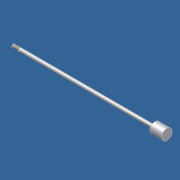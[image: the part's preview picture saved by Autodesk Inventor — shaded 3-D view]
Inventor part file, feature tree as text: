
AUTODESK INVENTOR PART (.ipt)
format: ipt  version: 2012 (Build 160160000, 160)  size: 124,928 bytes
history: native  units: in
note: dims shown in document units (in); Inventor stores cm internally (conversion verified against a paired STEP export)
features: other x84, revolve x3, sketch x3, thread x1
ambient origin geometry x8: Origin, YZ Plane, XZ Plane, XY Plane, X Axis, Y Axis, Z Axis, Center Point
bodies: Solid1 (feature_tree)
feature tree (91):
  revolve  "Revolution1"  Angle=360.0deg
  revolve  "Revolution2"  Angle=360.0deg
  thread  "Thread1"  [1 undecoded]
  revolve  "Revolution3"  [1 undecoded]
  other  "rod_cp_XY"
  other  "rod_cp_YZ"
  other  "rod_cp_ZX"
  other  "rod_cp_X"
  other  "rod_cp_Y"
  other  "rod_cp_Z"
  other  "rod_cp_Center"
  other  "to_rod_clevis_XY"
  other  "to_rod_clevis_YZ"
  other  "to_rod_clevis_ZX"
  other  "to_rod_clevis_X"
  other  "to_rod_clevis_Y"
  other  "to_rod_clevis_Z"
  other  "to_rod_clevis_Center"
  other  "rl2_XY"
  other  "rl2_YZ"
  other  "rl2_ZX"
  other  "rl2_X"
  other  "rl2_Y"
  other  "rl2_Z"
  other  "rl2_Center"
  other  "rl1_XY"
  other  "rl1_YZ"
  other  "rl1_ZX"
  other  "rl1_X"
  other  "rl1_Y"
  other  "rl1_Z"
  other  "rl1_Center"
  other  "thd1_XY"
  other  "thd1_YZ"
  other  "thd1_ZX"
  other  "thd1_X"
  other  "thd1_Y"
  other  "thd1_Z"
  other  "thd1_Center"
  other  "thd2_XY"
  other  "thd2_YZ"
  other  "thd2_ZX"
  other  "thd2_X"
  other  "thd2_Y"
  other  "thd2_Z"
  other  "thd2_Center"
  other  "dia1_XY"
  other  "dia1_YZ"
  other  "dia1_ZX"
  other  "dia1_X"
  other  "dia1_Y"
  other  "dia1_Z"
  other  "dia1_Center"
  other  "dia2_XY"
  other  "dia2_YZ"
  other  "dia2_ZX"
  other  "dia2_X"
  other  "dia2_Y"
  other  "dia2_Z"
  other  "dia2_Center"
  other  "hh1_XY"
  other  "hh1_YZ"
  other  "hh1_ZX"
  other  "hh1_X"
  other  "hh1_Y"
  other  "hh1_Z"
  other  "hh1_Center"
  other  "hh2_XY"
  other  "hh2_YZ"
  other  "hh2_ZX"
  other  "hh2_X"
  other  "hh2_Y"
  other  "hh2_Z"
  other  "hh2_Center"
  other  "dia12_XY"
  other  "dia12_YZ"
  other  "dia12_ZX"
  other  "dia12_X"
  other  "dia12_Y"
  other  "dia12_Z"
  other  "dia12_Center"
  other  "dia22_XY"
  other  "dia22_YZ"
  other  "dia22_ZX"
  other  "dia22_X"
  other  "dia22_Y"
  other  "dia22_Z"
  other  "dia22_Center"
  sketch  "Sketch_1"  dims[d0=360.0deg d1=360.0deg]
  sketch  "Sketch_3"  dims[d2=0.5in d3=9.594in d4=360.0deg]
  sketch  "Sketch_30"
note: 2 required parameter values undecoded (feature->parameter linkage not recoverable at this tier; creation-order binding heuristic only, values carry confidence <= 0.55)
